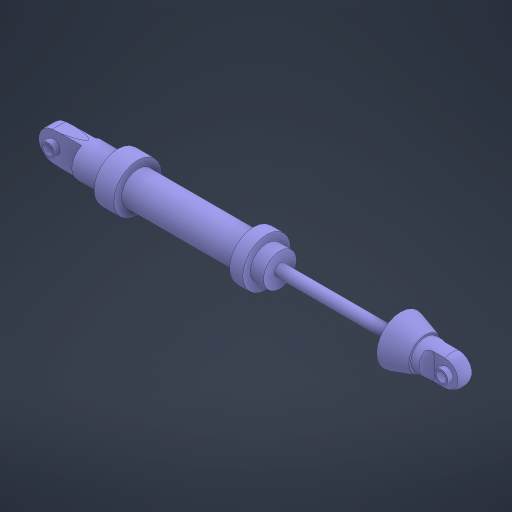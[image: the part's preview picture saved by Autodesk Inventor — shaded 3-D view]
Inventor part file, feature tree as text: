
AUTODESK INVENTOR PART (.ipt)
format: ipt  version: 2024 (Build 280153000, 153)  size: 343,552 bytes
history: native  units: mm
features: sketch x8, extrude x7, fillet x2, other x1, revolve x1, projected_geometry x1
ambient origin geometry x8: Origin, YZ Plane, XZ Plane, XY Plane, X Axis, Y Axis, Z Axis, Center Point
bodies: Body1 (feature_tree)
feature tree (20):
  other  "Твердое тело1"
  revolve  "Вращение1"
  extrude  "Выдавливание1"  Depth=10.0mm
  extrude  "Выдавливание2"  TaperAngle=90.0deg  [1 undecoded]
  extrude  "Выдавливание3"  Depth=6.0mm
  extrude  "Выдавливание5"  Depth=102.0mm
  extrude  "Выдавливание6"  Depth=36.5mm
  fillet  "Сопряжение1"  Radius=15.0mm
  fillet  "Сопряжение2"  Radius=54.0mm
  extrude  "Выдавливание7"  Depth=4.0mm
  extrude  "Выдавливание8"  Depth=14.5mm
  sketch  "Эскиз1"
  sketch  "Эскиз2"
  sketch  "Эскиз3"
  projected_geometry  "Спроецированная петля1"
  sketch  "Эскиз4"
  sketch  "Эскиз7"
  sketch  "Эскиз8"
  sketch  "Эскиз9"
  sketch  "Эскиз10"
note: 1 required parameter value undecoded (feature->parameter linkage not recoverable at this tier; creation-order binding heuristic only, values carry confidence <= 0.55)
